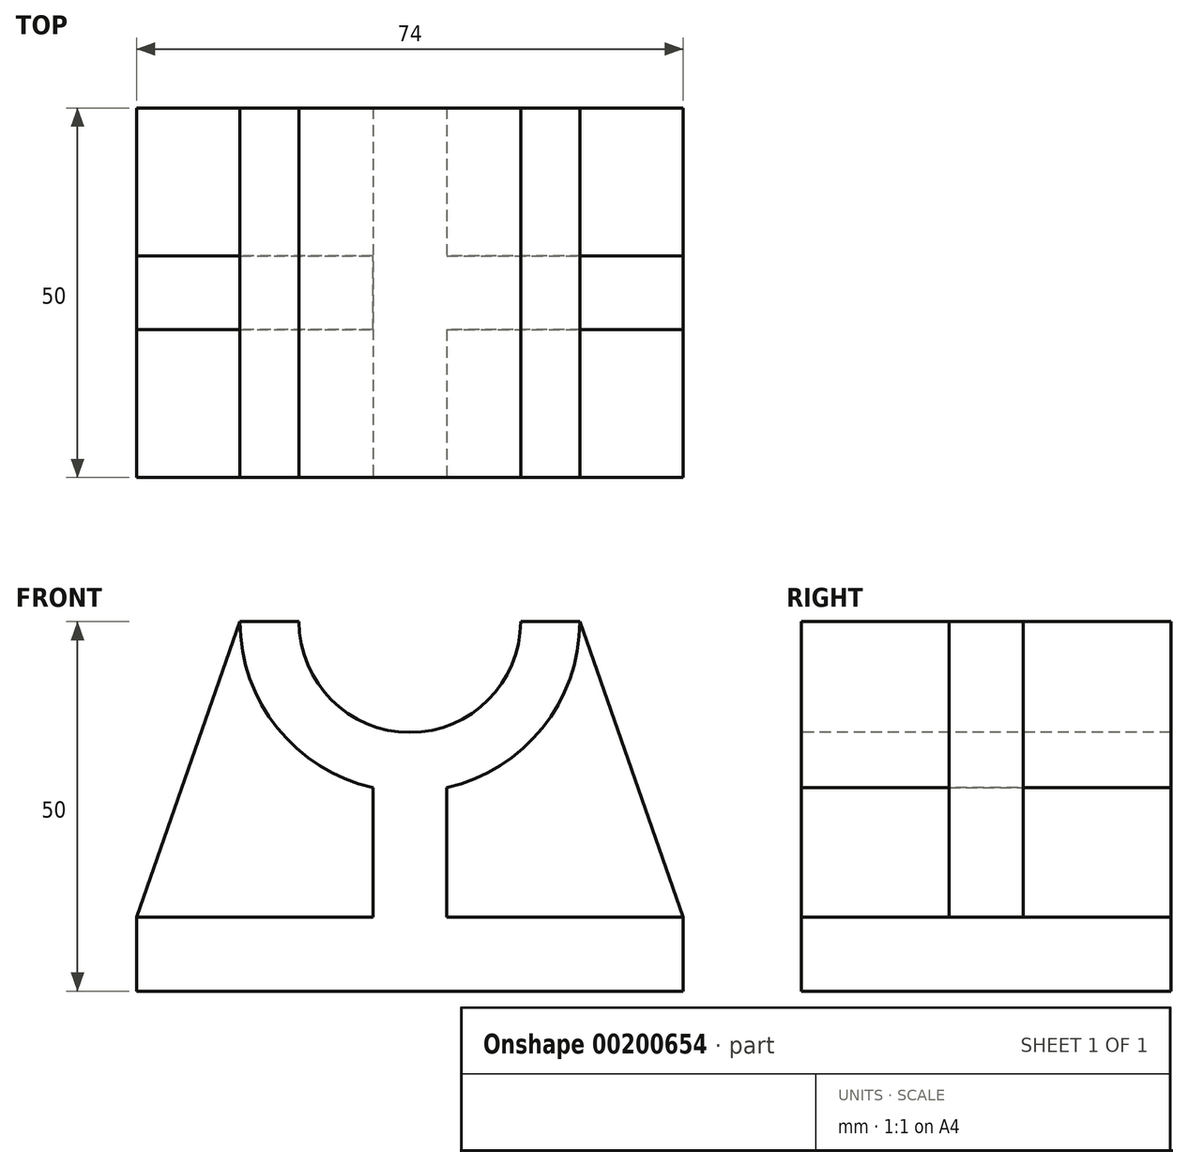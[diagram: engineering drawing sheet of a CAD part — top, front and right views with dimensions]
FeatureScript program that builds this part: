
annotation { "Feature Type Name" : "Feature", "Feature Type Description" : "" }
export const myFeature = defineFeature(function(context is Context, id is Id, definition is map)
    precondition{}
    {
        {
            var Q0;
            Q0=qCreatedBy(makeId("Front.planeOp"),FACE);
            var sketch = newSketch(context, id + "F0", { "sketchPlane" : qUnion([Q0])});
            skLineSegment(sketch, "E0", {"start": v(-37, 0) * mm, "end": v(37, 0) * mm});
            skLineSegment(sketch, "E1", {"start": v(37, 0) * mm, "end": v(37, 10) * mm});
            skLineSegment(sketch, "E2", {"start": v(37, 10) * mm, "end": v(5, 10) * mm});
            skLineSegment(sketch, "E3", {"start": v(5, 10) * mm, "end": v(5, 27) * mm});
            skLineSegment(sketch, "E4", {"start": v(-5, 23.14) * mm, "end": v(-5, 10) * mm});
            skLineSegment(sketch, "E5", {"start": v(-5, 10) * mm, "end": v(-37, 10) * mm});
            skLineSegment(sketch, "E6", {"start": v(-37, 10) * mm, "end": v(-37, 0) * mm});
            skLineSegment(sketch, "E7", {"start": v(0, 0) * mm, "end": v(0, 27) * mm});
            skArc(sketch, "E8", {"start": v(5, 27.55) * mm, "mid": v(17.94, 35.61) * mm, "end": v(23, 50) * mm});
            skArc(sketch, "E9", {"start": v(-15, 50) * mm, "mid": v(0, 35) * mm, "end": v(15, 50) * mm});
            skLineSegment(sketch, "E10", {"start": v(-5, 23.14) * mm, "end": v(-5, 27.55) * mm});
            skLineSegment(sketch, "E11", {"start": v(5, 27) * mm, "end": v(5, 27.55) * mm});
            skLineSegment(sketch, "E12", {"start": v(-15, 50) * mm, "end": v(-23, 50) * mm});
            skLineSegment(sketch, "E13", {"start": v(-23, 50) * mm, "end": v(-15, 50) * mm});
            skArc(sketch, "E14.trimOffspring", {"start": v(-23, 50) * mm, "mid": v(-17.94, 35.61) * mm, "end": v(-5, 27.55) * mm});
            skLineSegment(sketch, "E15.trimOffspring", {"start": v(15, 50) * mm, "end": v(23, 50) * mm});
            skSolve(sketch);
        }
        {
            var Q0;
            Q0 = qSketchRegion(id + "F0", true);
            extrude(context, id + "F1", {"entities" : qUnion([Q0]), "endBound" : BoundingType.SYMMETRIC, "oppositeDirection" : true, "depth" : 50 * mm});
        }
        {
            var Q0;
            Q0=qCreatedBy(makeId("Front.planeOp"),FACE);
            var sketch = newSketch(context, id + "F2", { "sketchPlane" : qUnion([Q0])});
            skArc(sketch, "E16.0", {"start": v(-23, 50) * mm, "mid": v(-17.94, 35.61) * mm, "end": v(-5, 27.55) * mm});
            skPoint(sketch, "E17.0", {"position": v(-5, 18.78) * mm});
            skLineSegment(sketch, "E18.0", {"start": v(-5, 10) * mm, "end": v(-5, 27.55) * mm});
            skPoint(sketch, "E19.0", {"position": v(-21, 10) * mm});
            skLineSegment(sketch, "E20.0", {"start": v(-5, 10) * mm, "end": v(-37, 10) * mm});
            skLineSegment(sketch, "E21", {"start": v(-23, 50) * mm, "end": v(-37, 10) * mm});
            skSolve(sketch);
        }
        {
            var Q0;
            Q0 = qSketchRegion(id + "F2", true);
            extrude(context, id + "F3", {"entities" : qUnion([Q0]), "endBound" : BoundingType.SYMMETRIC, "depth" : 10 * mm});
        }
        {
            var Q0;
            Q0=qCreatedBy(makeId("Front.planeOp"),FACE);
            var sketch = newSketch(context, id + "F4", { "sketchPlane" : qUnion([Q0])});
            skArc(sketch, "E22.0", {"start": v(5, 27.55) * mm, "mid": v(17.94, 35.61) * mm, "end": v(23, 50) * mm});
            skLineSegment(sketch, "E23.0", {"start": v(5, 10) * mm, "end": v(5, 27.55) * mm});
            skLineSegment(sketch, "E24.0", {"start": v(37, 10) * mm, "end": v(5, 10) * mm});
            skLineSegment(sketch, "E25", {"start": v(23, 50) * mm, "end": v(37, 10) * mm});
            skSolve(sketch);
        }
        {
            var Q0;
            Q0 = qSketchRegion(id + "F4", true);
            extrude(context, id + "F5", {"entities" : qUnion([Q0]), "operationType" : NewBodyOperationType.ADD, "endBound" : BoundingType.SYMMETRIC, "depth" : 10 * mm});
        }
    });
